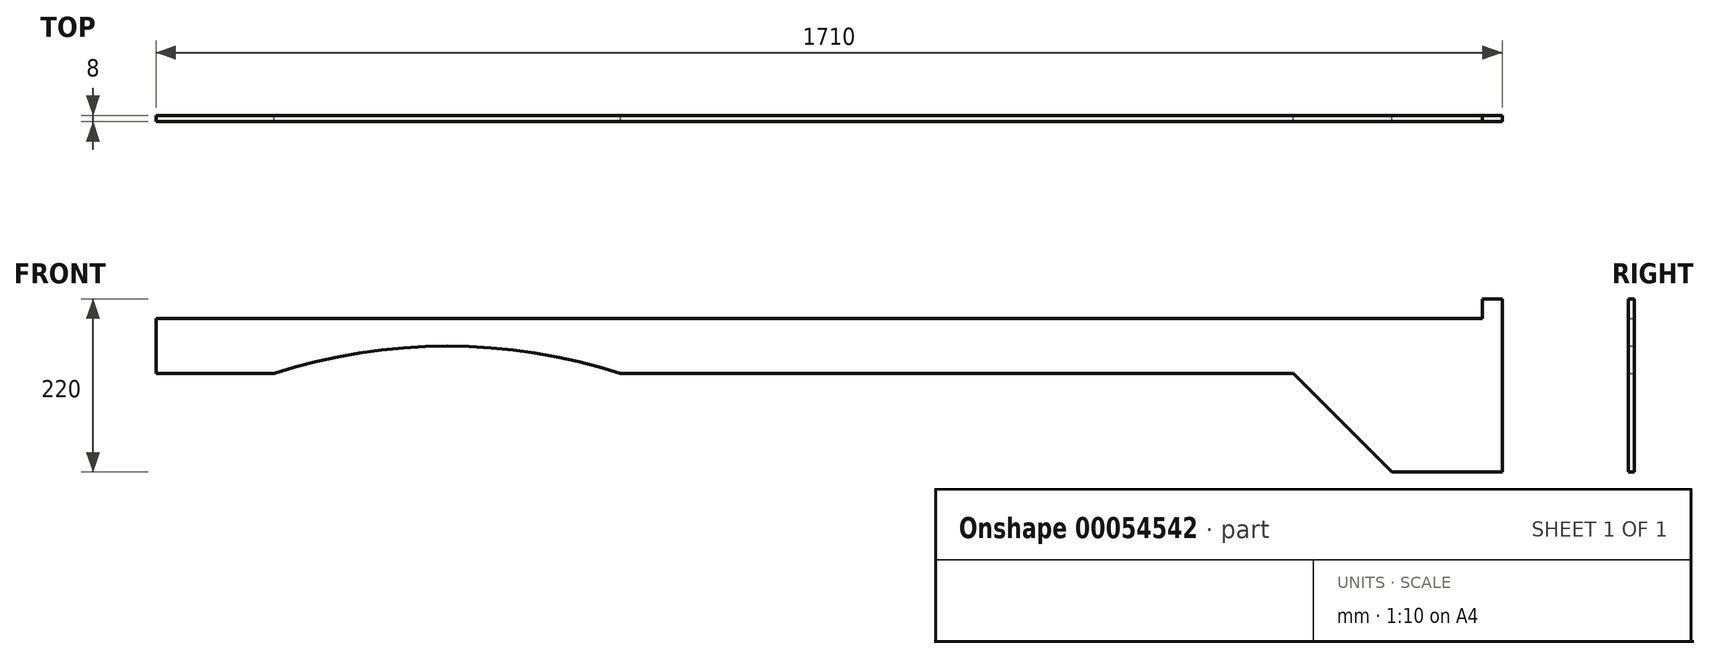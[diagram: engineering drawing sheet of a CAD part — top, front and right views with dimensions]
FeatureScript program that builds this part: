
annotation { "Feature Type Name" : "Feature", "Feature Type Description" : "" }
export const myFeature = defineFeature(function(context is Context, id is Id, definition is map)
    precondition{}
    {
        {
            var Q0;
            Q0=qCreatedBy(makeId("Front.planeOp"),FACE);
            var sketch = newSketch(context, id + "F0", { "sketchPlane" : qUnion([Q0])});
            skLineSegment(sketch, "E0.bottom", {"start": v(0, 0) * mm, "end": v(1710, 0) * mm});
            skLineSegment(sketch, "E0.top", {"start": v(0, -70) * mm, "end": v(1710, -70) * mm});
            skLineSegment(sketch, "E0.left", {"start": v(0, 0) * mm, "end": v(0, -70) * mm});
            skLineSegment(sketch, "E0.right", {"start": v(1710, 0) * mm, "end": v(1710, -70) * mm});
            skLineSegment(sketch, "E1", {"start": v(1710, -70) * mm, "end": v(1710, -195) * mm});
            skLineSegment(sketch, "E2", {"start": v(1710, -195) * mm, "end": v(1570, -195) * mm});
            skLineSegment(sketch, "E3", {"start": v(1570, -195) * mm, "end": v(1445, -70) * mm});
            skLineSegment(sketch, "E4", {"start": v(1710, 0) * mm, "end": v(1710, 25) * mm});
            skLineSegment(sketch, "E5", {"start": v(1710, 25) * mm, "end": v(1685, 25) * mm});
            skLineSegment(sketch, "E6", {"start": v(1685, 25) * mm, "end": v(1685, 0) * mm});
            skArc(sketch, "E7", {"start": v(590, -70) * mm, "mid": v(370, -35) * mm, "end": v(150, -70) * mm});
            skSolve(sketch);
        }
        {
            var Q0;
            {var subQ3=sQuery(id+"F0.wireOp",EDGE,"E0.left");Q0=makeQuery(id+"F0.imprint","IMPRINT",FACE,{"disambiguationData":[TD([[makeQuery(id+"F0.imprint","IMPRINT",EDGE,{"derivedFrom":subQ3}),1.0]])]});}
            var Q1;
            {var subQ0=sQuery(id+"F0.wireOp",EDGE,"E1");Q1=makeQuery(id+"F0.imprint","IMPRINT",FACE,{"disambiguationData":[TD([[makeQuery(id+"F0.imprint","IMPRINT",EDGE,{"derivedFrom":subQ0}),-1.0]])]});}
            var Q2;
            {var subQ0=sQuery(id+"F0.wireOp",EDGE,"E4");Q2=makeQuery(id+"F0.imprint","IMPRINT",FACE,{"disambiguationData":[TD([[makeQuery(id+"F0.imprint","IMPRINT",EDGE,{"derivedFrom":subQ0}),1.0]])]});}
            extrude(context, id + "F1", {"entities" : qUnion([Q0, Q1, Q2]), "depth" : 8 * mm});
        }
    });
